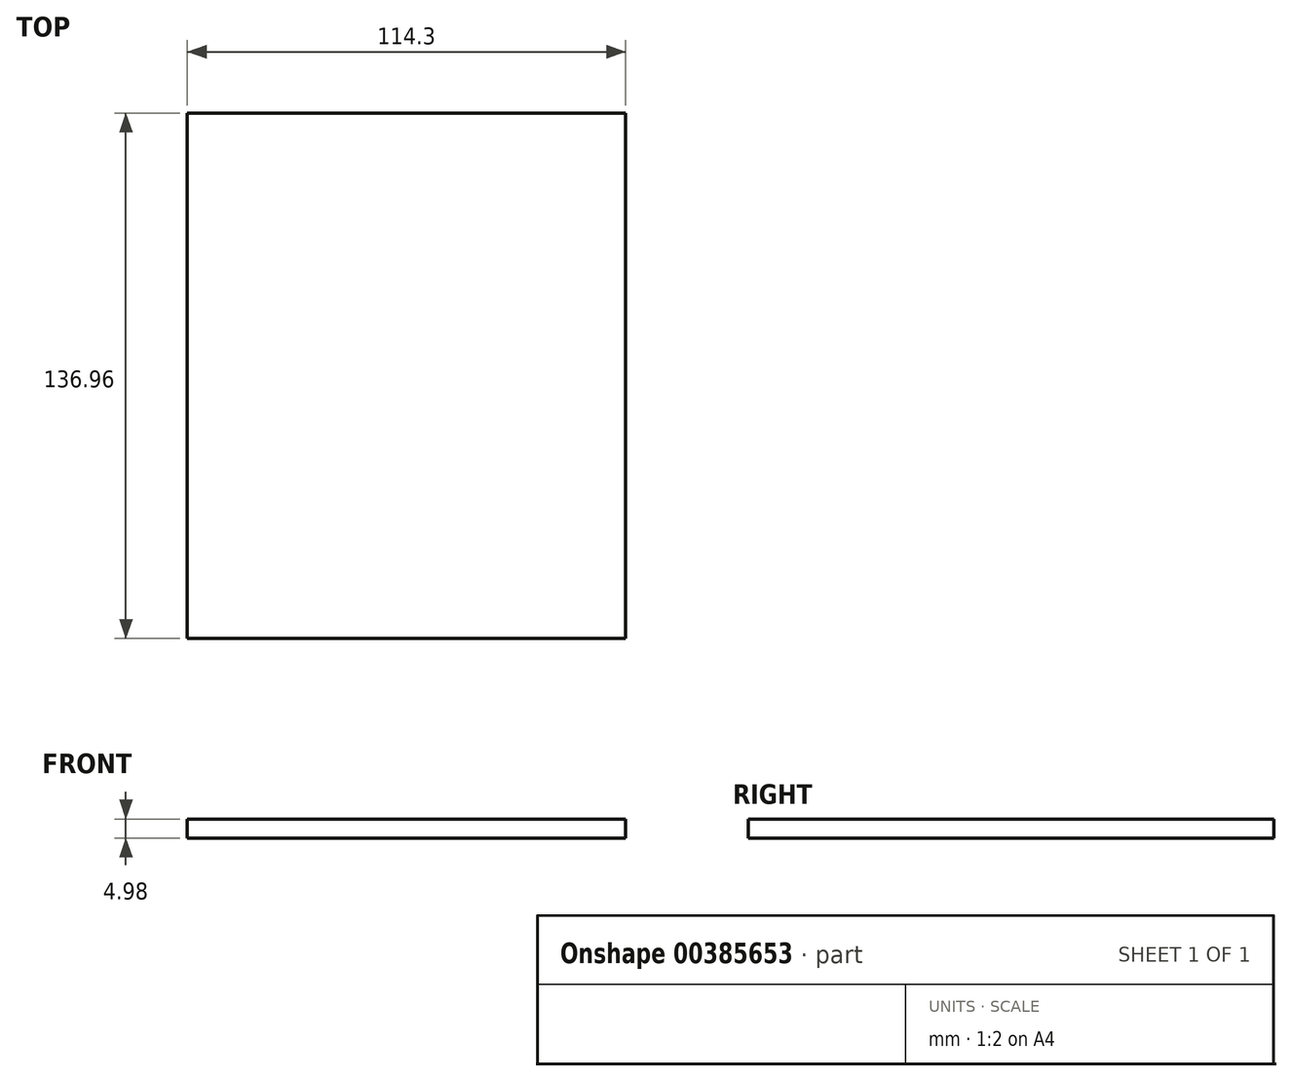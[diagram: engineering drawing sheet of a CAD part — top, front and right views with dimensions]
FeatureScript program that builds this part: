
annotation { "Feature Type Name" : "Feature", "Feature Type Description" : "" }
export const myFeature = defineFeature(function(context is Context, id is Id, definition is map)
    precondition{}
    {
        {
            var Q0;
            Q0=qCreatedBy(makeId("Top.planeOp"),FACE);
            var sketch = newSketch(context, id + "F0", { "sketchPlane" : qUnion([Q0])});
            skLineSegment(sketch, "E0.bottom", {"start": v(57.15, 68.48) * mm, "end": v(-57.15, 68.48) * mm});
            skLineSegment(sketch, "E0.top", {"start": v(57.15, -68.48) * mm, "end": v(-57.15, -68.48) * mm});
            skLineSegment(sketch, "E0.left", {"start": v(57.15, 68.48) * mm, "end": v(57.15, -68.48) * mm});
            skLineSegment(sketch, "E0.right", {"start": v(-57.15, 68.48) * mm, "end": v(-57.15, -68.48) * mm});
            skPoint(sketch, "E0.middle", {"position": v(0, 0) * mm});
            skSolve(sketch);
        }
        {
            var Q0;
            Q0=qSketchRegion(id+"F0",true);
            extrude(context, id + "F1", {"entities" : qUnion([Q0]), "depth" : 4.98 * mm});
        }
    });
